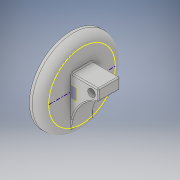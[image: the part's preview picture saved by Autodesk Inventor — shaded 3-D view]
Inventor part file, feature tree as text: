
AUTODESK INVENTOR PART (.ipt)
format: ipt  version: 2017 (Build 210142000, 142)  size: 195,584 bytes
history: native  units: in
note: dims shown in document units (in); Inventor stores cm internally (conversion verified against a paired STEP export)
features: sketch x3, extrude x2, fillet x2, plane x2
ambient origin geometry x8: Origin, YZ Plane, XZ Plane, XY Plane, X Axis, Y Axis, Z Axis, Center Point
bodies: Solid1 (feature_tree)
feature tree (9):
  extrude  "Extrusion1"  Depth=0.7874in TaperAngle=0.0deg
  fillet  "Fillet1"  Radius=0.5906in
  sketch  "Sketch2"  dims[d5=-0.7874in d6=3.5433in d9=0.7874in]
  plane  "Work Plane2"
  extrude  "Extrusion2"  Depth=3.5433in
  fillet  "Fillet2"  Radius=0.7874in
  sketch  "Sketch1"  dims[d0=6.0in d1=0.7874in d2=0.0in d3=0.5906in]
  plane  "Work Plane1"
  sketch  "Sketch3"  dims[d10=0.1969in d11=0.1969in d12=0.1969in d13=1.9685in d14=2.9528in d15=1.5748in d16=0.0in d17=0.0787in]
